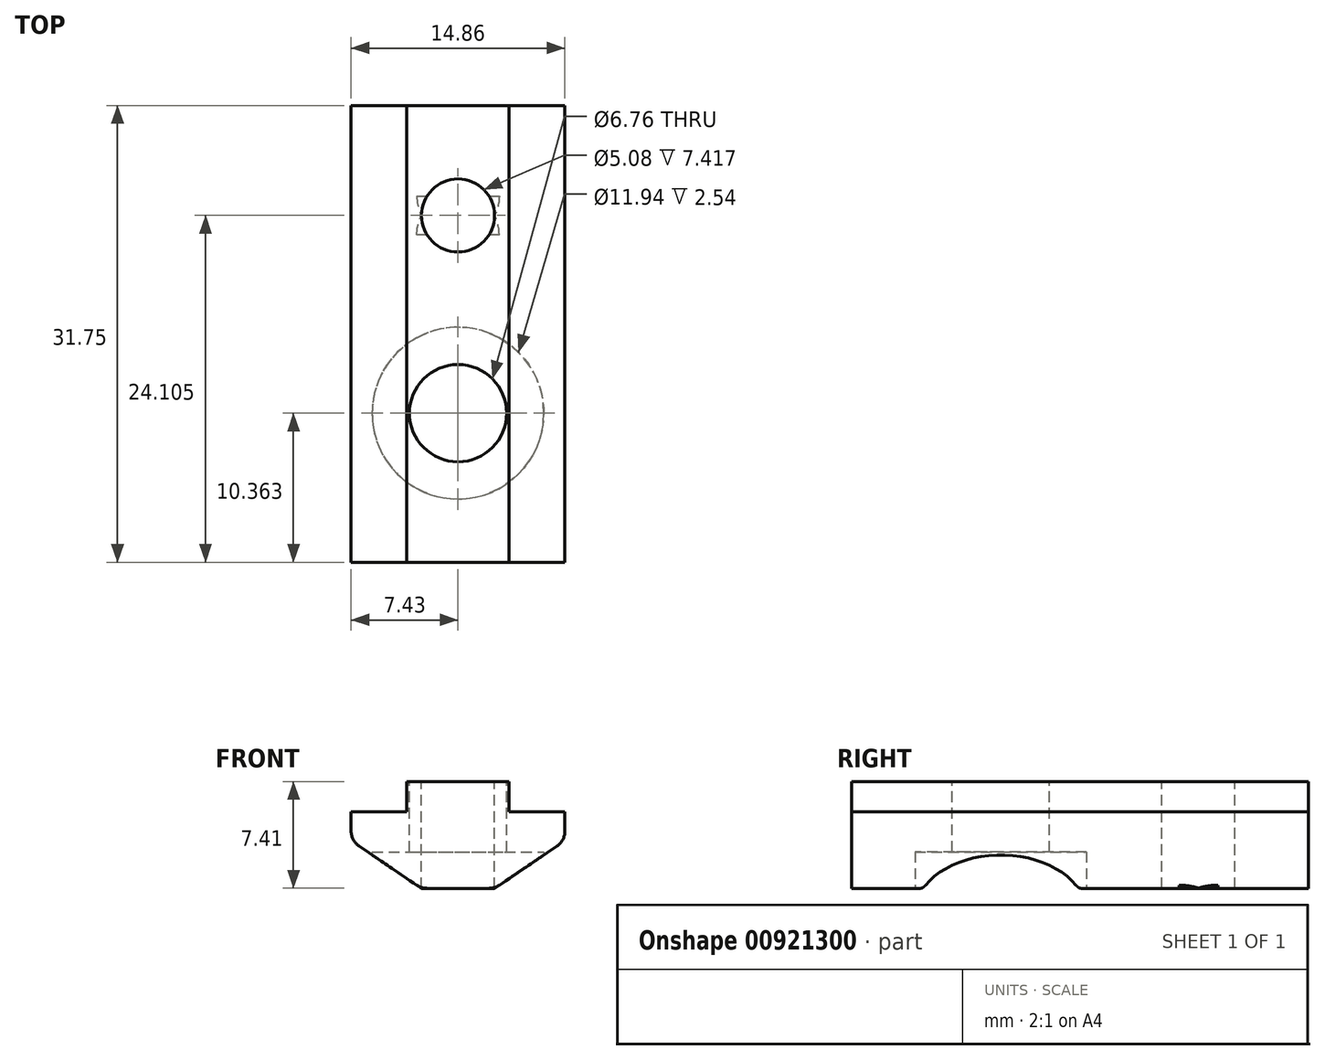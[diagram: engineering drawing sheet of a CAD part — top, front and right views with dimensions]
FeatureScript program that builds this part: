
annotation { "Feature Type Name" : "Feature", "Feature Type Description" : "" }
export const myFeature = defineFeature(function(context is Context, id is Id, definition is map)
    precondition{}
    {
        {
            var Q0;
            Q0=qCreatedBy(makeId("Front.planeOp"),FACE);
            var sketch = newSketch(context, id + "F0", { "sketchPlane" : qUnion([Q0])});
            skLineSegment(sketch, "E0.bottom", {"start": v(-3.56, 2.08) * mm, "end": v(3.56, 2.08) * mm});
            skLineSegment(sketch, "E0.left", {"start": v(-3.56, 2.08) * mm, "end": v(-3.56, 0) * mm});
            skLineSegment(sketch, "E0.right", {"start": v(3.56, 2.08) * mm, "end": v(3.56, 0) * mm});
            skLineSegment(sketch, "E1.bottom", {"start": v(-7.43, 0) * mm, "end": v(-3.56, 0) * mm});
            skLineSegment(sketch, "E1.left", {"start": v(-7.43, 0) * mm, "end": v(-7.43, -2.03) * mm});
            skLineSegment(sketch, "E1.right", {"start": v(7.43, 0) * mm, "end": v(7.43, -2.03) * mm});
            skLineSegment(sketch, "E2.top", {"start": v(-2.54, -5.33) * mm, "end": v(2.54, -5.33) * mm});
            skLineSegment(sketch, "E3.trimOffspring", {"start": v(3.56, 0) * mm, "end": v(7.43, 0) * mm});
            skLineSegment(sketch, "E4", {"start": v(-7.43, -2.03) * mm, "end": v(-2.54, -5.33) * mm});
            skLineSegment(sketch, "E5", {"start": v(7.43, -2.03) * mm, "end": v(2.54, -5.33) * mm});
            skSolve(sketch);
        }
        {
            var Q0;
            Q0=makeQuery(id+"F0.imprint","IMPRINT",FACE,{"disambiguationData":[TD([[makeQuery(id+"F0.imprint","IMPRINT",EDGE,{"derivedFrom":sQuery(id+"F0.wireOp",EDGE,"E0.bottom")}),-1.0]])]});
            var Q1;
            {var subQ0=sQuery(id+"F0.wireOp",EDGE,"E1.left");Q1=makeQuery(id+"F0.imprint","IMPRINT",FACE,{"disambiguationData":[TD([[makeQuery(id+"F0.imprint","IMPRINT",EDGE,{"derivedFrom":subQ0}),1.0]])]});}
            var Q2;
            Q2=makeQuery(id+"F0.imprint","IMPRINT",FACE,{"disambiguationData":[TD([[makeQuery(id+"F0.imprint","IMPRINT",EDGE,{"derivedFrom":sQuery(id+"F0.wireOp",EDGE,"E2.bottom")}),-1.0]])]});
            extrude(context, id + "F1", {"entities" : qUnion([Q0, Q1, Q2]), "depth" : 31.75 * mm, "offsetDistance" : 25.4 * mm});
        }
        {
            var Q0;
            Q0=makeQuery(id+"F1.opExtrude","SWEPT_FACE",FACE,{"disambiguationData":[OSD([sQuery(id+"F0.wireOp",EDGE,"E0.bottom")])]});
            var sketch = newSketch(context, id + "F2", { "sketchPlane" : qUnion([Q0])});
            skCircle(sketch, "E6", {"center": v(0, -21.39) * mm, "radius": 3.38 * mm});
            skCircle(sketch, "E7", {"center": v(0, -7.65) * mm, "radius": 2.54 * mm});
            skPoint(sketch, "E7.centerSnap0", {"position": v(0, 0) * mm});
            skSolve(sketch);
        }
        {
            var Q0;
            Q0=makeQuery(id+"F2.imprint","IMPRINT",FACE,{"disambiguationData":[TD([[makeQuery(id+"F2.imprint","IMPRINT",EDGE,{"derivedFrom":sQuery(id+"F2.wireOp",EDGE,"fXK3Fjaw-o3fJ-Wdds-udlc-ZsNGpqsiUqFL")}),1.0]])]});
            var Q1;
            Q1=makeQuery(id+"F2.imprint","IMPRINT",FACE,{"disambiguationData":[TD([[makeQuery(id+"F2.imprint","IMPRINT",EDGE,{"derivedFrom":sQuery(id+"F2.wireOp",EDGE,"E6")}),1.0]])]});
            var Q2;
            Q2=makeQuery(id+"F2.imprint","IMPRINT",FACE,{"disambiguationData":[TD([[makeQuery(id+"F2.imprint","IMPRINT",EDGE,{"derivedFrom":sQuery(id+"F2.wireOp",EDGE,"E7")}),1.0]])]});
            extrude(context, id + "F3", {"entities" : qUnion([Q0, Q1, Q2]), "operationType" : NewBodyOperationType.REMOVE, "oppositeDirection" : true, "depth" : 12.7 * mm, "offsetDistance" : 25.4 * mm});
        }
        {
            var Q0;
            Q0=makeQuery(id+"F1.opExtrude","SWEPT_EDGE",EDGE,{"disambiguationData":[OSD([sQuery(id+"F0.wireOp",EDGE,"E1.right"),sQuery(id+"F0.wireOp",EDGE,"E5")])]});
            var Q1;
            Q1=makeQuery(id+"F1.opExtrude","SWEPT_EDGE",EDGE,{"disambiguationData":[OSD([sQuery(id+"F0.wireOp",EDGE,"E2.top"),sQuery(id+"F0.wireOp",EDGE,"E5")])]});
            var Q2;
            Q2=makeQuery(id+"F1.opExtrude","SWEPT_EDGE",EDGE,{"disambiguationData":[OSD([sQuery(id+"F0.wireOp",EDGE,"E2.top"),sQuery(id+"F0.wireOp",EDGE,"E4")])]});
            var Q3;
            Q3=makeQuery(id+"F1.opExtrude","SWEPT_EDGE",EDGE,{"disambiguationData":[OSD([sQuery(id+"F0.wireOp",EDGE,"E1.left"),sQuery(id+"F0.wireOp",EDGE,"E4")])]});
            fillet(context, id + "F4", {"entities" : qUnion([Q0, Q1, Q2, Q3]), "radius" : 1.27 * mm, "tangentPropagation" : true, "allowEdgeOverflow" : false});
        }
        {
            var Q0;
            {var subQ0=sQuery(id+"F0.wireOp",EDGE,"E5");var subQ1=sQuery(id+"F0.wireOp",EDGE,"E4");var subQ2=sQuery(id+"F0.wireOp",EDGE,"E2.top");Q0=makeQuery(id+"F3.boolean.opBoolean","SPLIT",FACE,{"disambiguationData":[TD([makeQuery(id+"F1.opExtrude","CAP_FACE",FACE,{"disambiguationData":[OSD([sQuery(id+"F0.wireOp",EDGE,"E0.bottom"),sQuery(id+"F0.wireOp",EDGE,"E0.left"),sQuery(id+"F0.wireOp",EDGE,"E0.right"),sQuery(id+"F0.wireOp",EDGE,"E1.bottom"),sQuery(id+"F0.wireOp",EDGE,"E1.left"),sQuery(id+"F0.wireOp",EDGE,"E1.right"),subQ2,sQuery(id+"F0.wireOp",EDGE,"E3.trimOffspring"),subQ1,subQ0])],"isStart":false}),makeQuery(id+"F1.opExtrude","SWEPT_FACE",FACE,{"disambiguationData":[OSD([subQ1])]}),makeQuery(id+"F1.opExtrude","SWEPT_FACE",FACE,{"disambiguationData":[OSD([subQ0])]}),makeQuery(id+"F3.opExtrude","SWEPT_FACE",FACE,{"disambiguationData":[OSD([sQuery(id+"F2.wireOp",EDGE,"E6")])]})])],"derivedFrom":makeQuery(id+"F1.opExtrude","SWEPT_FACE",FACE,{"disambiguationData":[OSD([subQ2])]})});}
            var sketch = newSketch(context, id + "F5", { "sketchPlane" : qUnion([Q0])});
            skCircle(sketch, "E8", {"center": v(0, 21.39) * mm, "radius": 5.97 * mm});
            skSolve(sketch);
        }
        {
            var Q0;
            Q0 = qSketchRegion(id + "F5", true);
            extrude(context, id + "F6", {"entities" : qUnion([Q0]), "operationType" : NewBodyOperationType.REMOVE, "oppositeDirection" : true, "depth" : 2.54 * mm, "offsetDistance" : 25.4 * mm});
        }
    });
